# Revit family: portal_deceuninck_shema-c
name_source: partatom
category: Doors
revit_build: Autodesk Revit 2016 (Build: 20150506_1715(x64)
units: mm (PartAtom-declared; Revit-internal decimal feet)

## family parameters
Always vertical = Yes
Cut with Voids When Loaded = No
Host = Wall
OmniClass Number = 23.30.20.00
OmniClass Title = Windows
Room Calculation Point = No
Shared = No

## types (1)
- Портал HST 76 - схема C
    Analytic Construction = <Нет>
    Fire Rating = Е-60
    Height = 0 mm  [stored 0 ft]
    Rough Height = 0 mm  [stored 0 ft]
    Rough Width = 0 mm  [stored 0 ft]
    Rед = 1.0000 (m²·K)/W
    Rпрофиля = 0.7700 (m²·K)/W
    Rстеклопакета = 0.7800 (m²·K)/W
    Thickness = 0 mm  [stored 0 ft]
    Wall Closure = By host
    Width = 0 mm  [stored 0 ft]
    λ краевой зоны стеклопакета = 0.0600 (m²·K)/W
    Артикул рамы/армирование рамы = HS 176 / NA 57
    Артикул створки/армирование рстворки = HS 4761D  / NA 66
    ГОСТ = RAL-GZ 716/1
    Материал-Рама = <By Category>
    Материал-Стеклопакет = <By Category>
    Монтажный зазор.Боковой = 20 mm  [stored 0.0656168 ft]
    Наименование = Портал HST 76 Схема С
    Профильная система = HST 76
    Толщина стеклопакета = 48
    Ширина профиля = 76 mm  [stored 0.249344 ft]

note: [stored X ft] marks values corroborated as IEEE doubles in the binary element streams (Revit-internal decimal feet)

## geometry (parser evidence)
native form markers: Blend x4
no freeform markers — native parametric forms only
